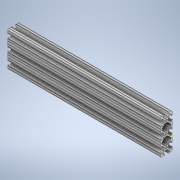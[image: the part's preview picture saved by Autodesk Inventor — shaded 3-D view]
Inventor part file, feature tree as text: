
AUTODESK INVENTOR PART (.ipt)
format: ipt  version: 2020 (Build 240168000, 168)  size: 381,952 bytes
history: native  units: in
note: dims shown in document units (in); Inventor stores cm internally (conversion verified against a paired STEP export)
features: sketch x2, extrude x1
ambient origin geometry x8: Origin, YZ Plane, XZ Plane, XY Plane, X Axis, Y Axis, Z Axis, Center Point
bodies: Solid1 (feature_tree)
feature tree (3):
  extrude  "Extrusion1"  [1 undecoded]
  sketch  "Sketch2"
  sketch  "Sketch1"  dims[d0=13.0in d1=0.0in]
note: 1 required parameter value undecoded (feature->parameter linkage not recoverable at this tier; creation-order binding heuristic only, values carry confidence <= 0.55)
